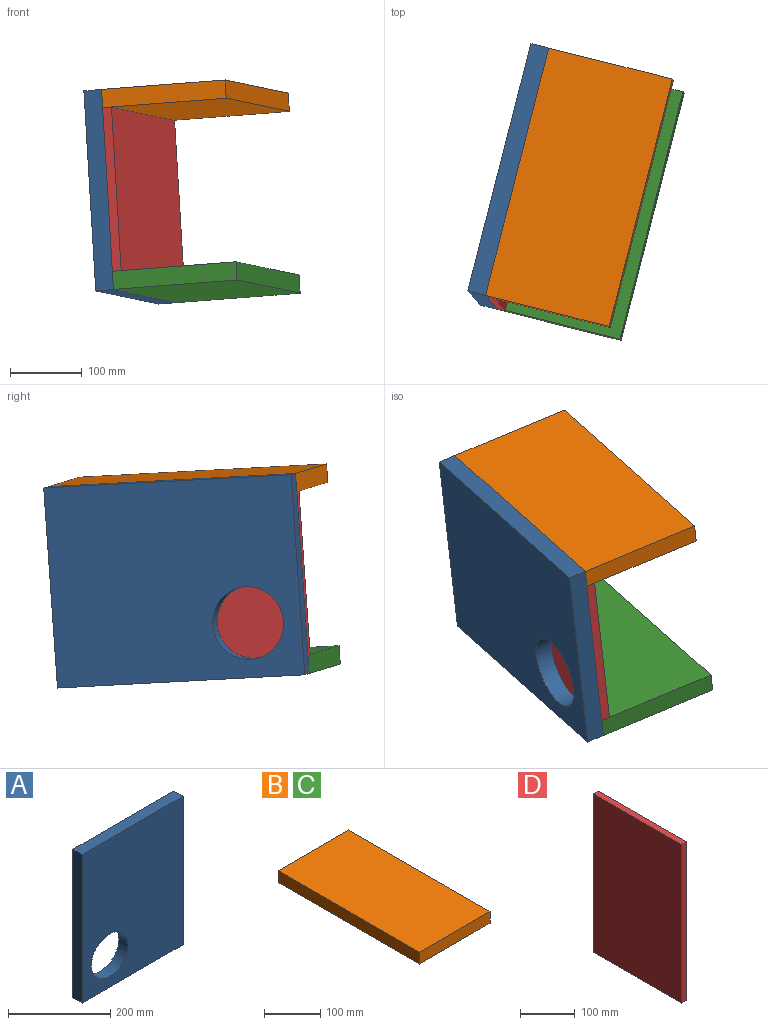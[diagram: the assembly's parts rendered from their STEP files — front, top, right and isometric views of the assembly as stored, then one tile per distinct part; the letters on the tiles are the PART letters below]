
ASSEMBLY  parts=4 mates=3
PART A: 7 faces, bbox 279.4x25.4x355.6 mm
  f0: plane 279.4x25.4mm, normal (0,0,-1), area 7096.8mm2, adj f1,f3,f4,f5
  f1: plane 355.6x25.4mm, normal (1,0,0), area 9032.2mm2, adj f0,f2,f4,f5
  f2: plane 279.4x25.4mm, normal (0,0,1), area 7096.8mm2, adj f1,f3,f4,f5
  f3: plane 355.6x25.4mm, normal (-1,0,0), area 9032.2mm2, adj f0,f2,f4,f5
  f4: plane 355.6x279.4mm, normal (0,-1,0), area 91247.3mm2, adj f0,f1,f2,f3,f6
  f5: plane 355.6x279.4mm, normal (0,1,0), area 91247.3mm2, adj f0,f1,f2,f3,f6
  f6: cylinder r=50.8mm len=101.6mm, axis (0,1,0), area 8107.3mm2, adj f4,f5
PART B: 6 faces, bbox 177.8x355.6x25.4 mm
  f0: plane 355.6x25.4mm, normal (-1,0,0), area 9032.2mm2, adj f1,f3,f4,f5
  f1: plane 177.8x25.4mm, normal (0,-1,0), area 4516.1mm2, adj f0,f2,f4,f5
  f2: plane 355.6x25.4mm, normal (1,0,0), area 9032.2mm2, adj f1,f3,f4,f5
  f3: plane 177.8x25.4mm, normal (0,1,0), area 4516.1mm2, adj f0,f2,f4,f5
  f4: plane 355.6x177.8mm, normal (0,0,1), area 63225.7mm2, adj f0,f1,f2,f3
  f5: plane 355.6x177.8mm, normal (0,0,-1), area 63225.7mm2, adj f0,f1,f2,f3
PART C: same geometry as B
PART D: 6 faces, bbox 12.7x228.6x355.6 mm
  f0: plane 355.6x12.7mm, normal (0,-1,0), area 4516.1mm2, adj f1,f3,f4,f5
  f1: plane 228.6x12.7mm, normal (0,0,-1), area 2903.2mm2, adj f0,f2,f4,f5
  f2: plane 355.6x12.7mm, normal (0,1,0), area 4516.1mm2, adj f1,f3,f4,f5
  f3: plane 228.6x12.7mm, normal (0,0,1), area 2903.2mm2, adj f0,f2,f4,f5
  f4: plane 355.6x228.6mm, normal (1,0,0), area 81290.2mm2, adj f0,f1,f2,f3
  f5: plane 355.6x228.6mm, normal (-1,0,0), area 81290.2mm2, adj f0,f1,f2,f3
PLACE A rot(axis=(-0.61,-0.51,-0.61),132.6deg) t=(13.26,74.25,12.23)mm
PLACE B rot(axis=(0.12,0.99,-0.03),176.1deg) t=(90.97,62.22,157.95)mm
PLACE C rot(axis=(0.99,-0.12,0.03),176.5deg) t=(106.02,44.85,-95.01)mm
PLACE D rot(axis=(-0.98,0.09,-0.15),94.4deg) t=(13.26,74.25,12.23)mm
MATE fastened D.f5 <-> A.f5  axis (-0.97,0.24,-0.07) through (57.15,246.3,3.03)mm
MATE fastened C.f0 <-> A.f5  axis (-0.97,0.24,-0.07) through (21.54,64.69,-126.9)mm
MATE fastened B.f2 <-> A.f5  axis (-0.97,0.24,-0.07) through (4.98,83.8,151.35)mm
